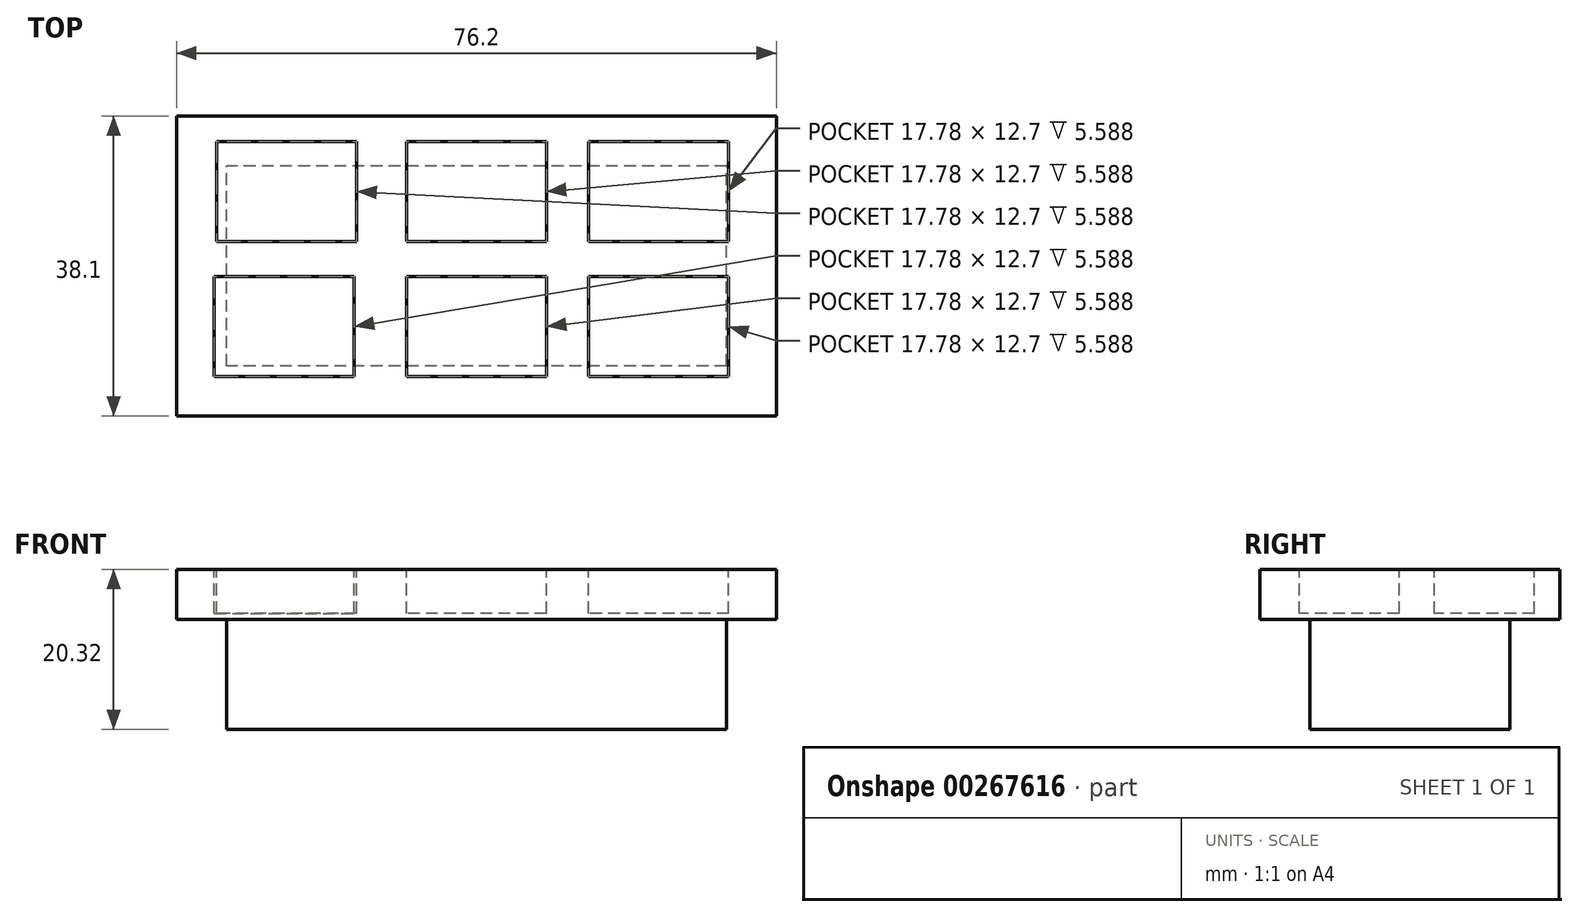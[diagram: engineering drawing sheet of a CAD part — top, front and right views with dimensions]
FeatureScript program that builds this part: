
annotation { "Feature Type Name" : "Feature", "Feature Type Description" : "" }
export const myFeature = defineFeature(function(context is Context, id is Id, definition is map)
    precondition{}
    {
        {
            var Q0;
            Q0=qCreatedBy(makeId("Top.planeOp"),FACE);
            var sketch = newSketch(context, id + "F0", { "sketchPlane" : qUnion([Q0])});
            skLineSegment(sketch, "E0.bottom", {"start": v(38.1, 19.05) * mm, "end": v(-38.1, 19.05) * mm});
            skLineSegment(sketch, "E0.top", {"start": v(38.1, -19.05) * mm, "end": v(-38.1, -19.05) * mm});
            skLineSegment(sketch, "E0.left", {"start": v(38.1, 19.05) * mm, "end": v(38.1, -19.05) * mm});
            skLineSegment(sketch, "E0.right", {"start": v(-38.1, 19.05) * mm, "end": v(-38.1, -19.05) * mm});
            skPoint(sketch, "E0.middle", {"position": v(0, 0) * mm});
            skSolve(sketch);
        }
        {
            var Q0;
            Q0 = qSketchRegion(id + "F0", true);
            extrude(context, id + "F1", {"entities" : qUnion([Q0]), "depth" : 20.32 * mm});
        }
        {
            var Q0;
            Q0=makeQuery(id+"F1.opExtrude","CAP_FACE",FACE,{"disambiguationData":[OSD([sQuery(id+"F0.wireOp",EDGE,"E0.bottom"),sQuery(id+"F0.wireOp",EDGE,"E0.top"),sQuery(id+"F0.wireOp",EDGE,"E0.left"),sQuery(id+"F0.wireOp",EDGE,"E0.right")])],"isStart":true});
            var sketch = newSketch(context, id + "F2", { "sketchPlane" : qUnion([Q0])});
            skLineSegment(sketch, "E1.bottom", {"start": v(31.75, 12.7) * mm, "end": v(-31.75, 12.7) * mm});
            skLineSegment(sketch, "E1.top", {"start": v(31.75, -12.7) * mm, "end": v(-31.75, -12.7) * mm});
            skLineSegment(sketch, "E1.left", {"start": v(31.75, 12.7) * mm, "end": v(31.75, -12.7) * mm});
            skLineSegment(sketch, "E1.right", {"start": v(-31.75, 12.7) * mm, "end": v(-31.75, -12.7) * mm});
            skPoint(sketch, "E1.middle", {"position": v(0, 0) * mm});
            skLineSegment(sketch, "E2", {"start": v(-31.75, 12.7) * mm, "end": v(-31.75, 19.05) * mm});
            skLineSegment(sketch, "E3", {"start": v(-31.75, 19.05) * mm, "end": v(-31.75, -12.7) * mm});
            skLineSegment(sketch, "E4", {"start": v(-31.75, -19.05) * mm, "end": v(-31.75, -12.7) * mm});
            skLineSegment(sketch, "E5", {"start": v(31.75, 12.7) * mm, "end": v(31.75, 19.05) * mm});
            skLineSegment(sketch, "E6", {"start": v(31.75, -12.7) * mm, "end": v(31.75, -19.05) * mm});
            skSolve(sketch);
        }
        {
            var Q0;
            {var subQ0=sQuery(id+"F2.wireOp",EDGE,"E4");Q0=makeQuery(id+"F2.imprint","IMPRINT",FACE,{"disambiguationData":[TD([[makeQuery(id+"F2.imprint","IMPRINT",EDGE,{"derivedFrom":subQ0}),1.0]])]});}
            var Q1;
            {var subQ0=sQuery(id+"F2.wireOp",EDGE,"E1.bottom");Q1=makeQuery(id+"F2.imprint","IMPRINT",FACE,{"disambiguationData":[TD([[makeQuery(id+"F2.imprint","IMPRINT",EDGE,{"derivedFrom":subQ0}),-1.0]])]});}
            var Q2;
            Q2=makeQuery(id+"F2.imprint","IMPRINT",FACE,{"disambiguationData":[TD([[makeQuery(id+"F2.imprint","IMPRINT",EDGE,{"derivedFrom":sQuery(id+"F2.wireOp",EDGE,"E1.left")}),1.0]])]});
            var Q3;
            Q3=makeQuery(id+"F2.imprint","IMPRINT",FACE,{"disambiguationData":[TD([[makeQuery(id+"F2.imprint","IMPRINT",EDGE,{"derivedFrom":sQuery(id+"F2.wireOp",EDGE,"E1.top")}),1.0]])]});
            extrude(context, id + "F3", {"entities" : qUnion([Q0, Q1, Q2, Q3]), "operationType" : NewBodyOperationType.REMOVE, "oppositeDirection" : true, "depth" : 13.97 * mm});
        }
        {
            var Q0;
            Q0=makeQuery(id+"F1.opExtrude","CAP_FACE",FACE,{"disambiguationData":[OSD([sQuery(id+"F0.wireOp",EDGE,"E0.bottom"),sQuery(id+"F0.wireOp",EDGE,"E0.top"),sQuery(id+"F0.wireOp",EDGE,"E0.left"),sQuery(id+"F0.wireOp",EDGE,"E0.right")])],"isStart":false});
            var sketch = newSketch(context, id + "F4", { "sketchPlane" : qUnion([Q0])});
            skLineSegment(sketch, "E7", {"start": v(-38.1, 9.49) * mm, "end": v(38.1, 9.49) * mm});
            skLineSegment(sketch, "E8.bottom", {"start": v(8.89, 15.84) * mm, "end": v(-8.9, 15.84) * mm});
            skLineSegment(sketch, "E8.top", {"start": v(8.9, 3.14) * mm, "end": v(-8.9, 3.14) * mm});
            skLineSegment(sketch, "E8.left", {"start": v(8.89, 15.84) * mm, "end": v(8.89, 3.14) * mm});
            skLineSegment(sketch, "E8.right", {"start": v(-8.9, 15.84) * mm, "end": v(-8.9, 3.14) * mm});
            skPoint(sketch, "E8.middle", {"position": v(0, 9.49) * mm});
            skLineSegment(sketch, "E9.bottom", {"start": v(-15.2, 15.84) * mm, "end": v(-32.98, 15.84) * mm});
            skLineSegment(sketch, "E9.top", {"start": v(-15.2, 3.14) * mm, "end": v(-32.98, 3.14) * mm});
            skLineSegment(sketch, "E9.left", {"start": v(-15.2, 15.84) * mm, "end": v(-15.2, 3.14) * mm});
            skLineSegment(sketch, "E9.right", {"start": v(-32.98, 15.84) * mm, "end": v(-32.98, 3.14) * mm});
            skPoint(sketch, "E9.middle", {"position": v(-24.09, 9.49) * mm});
            skLineSegment(sketch, "E10.bottom", {"start": v(32.03, 15.84) * mm, "end": v(14.25, 15.84) * mm});
            skLineSegment(sketch, "E10.top", {"start": v(32.03, 3.14) * mm, "end": v(14.25, 3.14) * mm});
            skLineSegment(sketch, "E10.left", {"start": v(32.03, 15.84) * mm, "end": v(32.03, 3.14) * mm});
            skLineSegment(sketch, "E10.right", {"start": v(14.25, 15.84) * mm, "end": v(14.25, 3.14) * mm});
            skPoint(sketch, "E10.middle", {"position": v(23.14, 9.49) * mm});
            skLineSegment(sketch, "E11", {"start": v(-15.2, 3.14) * mm, "end": v(-15.2, -19.05) * mm});
            skLineSegment(sketch, "E12", {"start": v(-8.9, 3.14) * mm, "end": v(-8.9, -19.05) * mm});
            skLineSegment(sketch, "E13", {"start": v(8.89, 3.14) * mm, "end": v(8.89, -19.05) * mm});
            skLineSegment(sketch, "E14", {"start": v(14.25, 3.14) * mm, "end": v(14.25, -19.05) * mm});
            skLineSegment(sketch, "E15", {"start": v(32.03, 3.14) * mm, "end": v(32.03, -19.05) * mm});
            skLineSegment(sketch, "E16", {"start": v(-38.1, -7.7) * mm, "end": v(38.1, -7.7) * mm});
            skPoint(sketch, "E16.startSnap0", {"position": v(-32.98, -7.7) * mm});
            skLineSegment(sketch, "E17.bottom", {"start": v(-33.3, -1.34) * mm, "end": v(-15.51, -1.34) * mm});
            skLineSegment(sketch, "E17.top", {"start": v(-33.3, -14.04) * mm, "end": v(-15.51, -14.04) * mm});
            skLineSegment(sketch, "E17.left", {"start": v(-33.3, -1.34) * mm, "end": v(-33.3, -14.04) * mm});
            skLineSegment(sketch, "E17.right", {"start": v(-15.51, -1.34) * mm, "end": v(-15.51, -14.04) * mm});
            skPoint(sketch, "E17.middle", {"position": v(-24.4, -7.7) * mm});
            skLineSegment(sketch, "E18.bottom", {"start": v(8.89, -1.34) * mm, "end": v(-8.9, -1.34) * mm});
            skLineSegment(sketch, "E18.top", {"start": v(8.89, -14.04) * mm, "end": v(-8.9, -14.04) * mm});
            skLineSegment(sketch, "E18.left", {"start": v(8.89, -1.34) * mm, "end": v(8.89, -14.04) * mm});
            skLineSegment(sketch, "E18.right", {"start": v(-8.9, -1.34) * mm, "end": v(-8.9, -14.04) * mm});
            skPoint(sketch, "E18.middle", {"position": v(0, -7.7) * mm});
            skLineSegment(sketch, "E19.bottom", {"start": v(32.03, -1.34) * mm, "end": v(14.25, -1.34) * mm});
            skLineSegment(sketch, "E19.top", {"start": v(32.03, -14.04) * mm, "end": v(14.25, -14.04) * mm});
            skLineSegment(sketch, "E19.left", {"start": v(32.03, -1.34) * mm, "end": v(32.03, -14.04) * mm});
            skLineSegment(sketch, "E19.right", {"start": v(14.25, -1.34) * mm, "end": v(14.25, -14.04) * mm});
            skPoint(sketch, "E19.middle", {"position": v(23.14, -7.7) * mm});
            skSolve(sketch);
        }
        {
            var Q0;
            {var subQ5=sQuery(id+"F4.wireOp",EDGE,"E10.bottom");Q0=makeQuery(id+"F4.imprint","IMPRINT",FACE,{"disambiguationData":[TD([[makeQuery(id+"F4.imprint","IMPRINT",EDGE,{"derivedFrom":subQ5}),1.0]])]});}
            var Q1;
            {var subQ5=sQuery(id+"F4.wireOp",EDGE,"E10.top");Q1=makeQuery(id+"F4.imprint","IMPRINT",FACE,{"disambiguationData":[TD([[makeQuery(id+"F4.imprint","IMPRINT",EDGE,{"derivedFrom":subQ5}),-1.0]])]});}
            var Q2;
            {var subQ5=sQuery(id+"F4.wireOp",EDGE,"E19.bottom");Q2=makeQuery(id+"F4.imprint","IMPRINT",FACE,{"disambiguationData":[TD([[makeQuery(id+"F4.imprint","IMPRINT",EDGE,{"derivedFrom":subQ5}),1.0]])]});}
            var Q3;
            {var subQ5=sQuery(id+"F4.wireOp",EDGE,"E19.top");Q3=makeQuery(id+"F4.imprint","IMPRINT",FACE,{"disambiguationData":[TD([[makeQuery(id+"F4.imprint","IMPRINT",EDGE,{"derivedFrom":subQ5}),-1.0]])]});}
            var Q4;
            {var subQ5=sQuery(id+"F4.wireOp",EDGE,"E18.top");Q4=makeQuery(id+"F4.imprint","IMPRINT",FACE,{"disambiguationData":[TD([[makeQuery(id+"F4.imprint","IMPRINT",EDGE,{"derivedFrom":subQ5}),-1.0]])]});}
            var Q5;
            {var subQ5=sQuery(id+"F4.wireOp",EDGE,"E18.bottom");Q5=makeQuery(id+"F4.imprint","IMPRINT",FACE,{"disambiguationData":[TD([[makeQuery(id+"F4.imprint","IMPRINT",EDGE,{"derivedFrom":subQ5}),1.0]])]});}
            var Q6;
            {var subQ5=sQuery(id+"F4.wireOp",EDGE,"E17.top");Q6=makeQuery(id+"F4.imprint","IMPRINT",FACE,{"disambiguationData":[TD([[makeQuery(id+"F4.imprint","IMPRINT",EDGE,{"derivedFrom":subQ5}),1.0]])]});}
            var Q7;
            {var subQ5=sQuery(id+"F4.wireOp",EDGE,"E17.bottom");Q7=makeQuery(id+"F4.imprint","IMPRINT",FACE,{"disambiguationData":[TD([[makeQuery(id+"F4.imprint","IMPRINT",EDGE,{"derivedFrom":subQ5}),-1.0]])]});}
            var Q8;
            {var subQ5=sQuery(id+"F4.wireOp",EDGE,"E9.top");Q8=makeQuery(id+"F4.imprint","IMPRINT",FACE,{"disambiguationData":[TD([[makeQuery(id+"F4.imprint","IMPRINT",EDGE,{"derivedFrom":subQ5}),-1.0]])]});}
            var Q9;
            {var subQ5=sQuery(id+"F4.wireOp",EDGE,"E9.bottom");Q9=makeQuery(id+"F4.imprint","IMPRINT",FACE,{"disambiguationData":[TD([[makeQuery(id+"F4.imprint","IMPRINT",EDGE,{"derivedFrom":subQ5}),1.0]])]});}
            var Q10;
            {var subQ5=sQuery(id+"F4.wireOp",EDGE,"E8.bottom");Q10=makeQuery(id+"F4.imprint","IMPRINT",FACE,{"disambiguationData":[TD([[makeQuery(id+"F4.imprint","IMPRINT",EDGE,{"derivedFrom":subQ5}),1.0]])]});}
            var Q11;
            {var subQ5=sQuery(id+"F4.wireOp",EDGE,"E8.top");Q11=makeQuery(id+"F4.imprint","IMPRINT",FACE,{"disambiguationData":[TD([[makeQuery(id+"F4.imprint","IMPRINT",EDGE,{"derivedFrom":subQ5}),-1.0]])]});}
            extrude(context, id + "F5", {"entities" : qUnion([Q0, Q1, Q2, Q3, Q4, Q5, Q6, Q7, Q8, Q9, Q10, Q11]), "operationType" : NewBodyOperationType.REMOVE, "oppositeDirection" : true, "depth" : 5.6 * mm});
        }
    });
